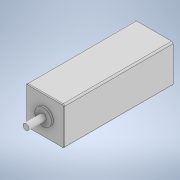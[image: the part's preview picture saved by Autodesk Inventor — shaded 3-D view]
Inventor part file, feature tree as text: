
AUTODESK INVENTOR PART (.ipt)
format: ipt  version: 2020 (Build 240168000, 168)  size: 125,952 bytes
history: native  units: mm
features: extrude x3, sketch x3, fillet x2
ambient origin geometry x8: Origin, YZ Plane, XZ Plane, XY Plane, X Axis, Y Axis, Z Axis, Center Point
bodies: Solid1 (feature_tree)
feature tree (8):
  extrude  "Extrusion1"  Depth=50.0mm
  extrude  "Extrusion2"  Depth=25.0mm
  extrude  "Extrusion3"  Depth=1.0mm
  fillet  "Fillet1"  Radius=2.4mm
  fillet  "Fillet2"  Radius=8.0mm
  sketch  "Sketch1"  dims[d0=50.0mm d1=50.0mm]
  sketch  "Sketch2"  dims[d2=25.0mm d3=25.0mm]
  sketch  "Sketch3"  dims[d4=143.0mm d5=0.0mm d7=22.0mm d8=2.4mm d9=0.0mm d10=8.0mm d11=22.5mm d12=0.0mm d13=2.0mm d14=1.0mm]
